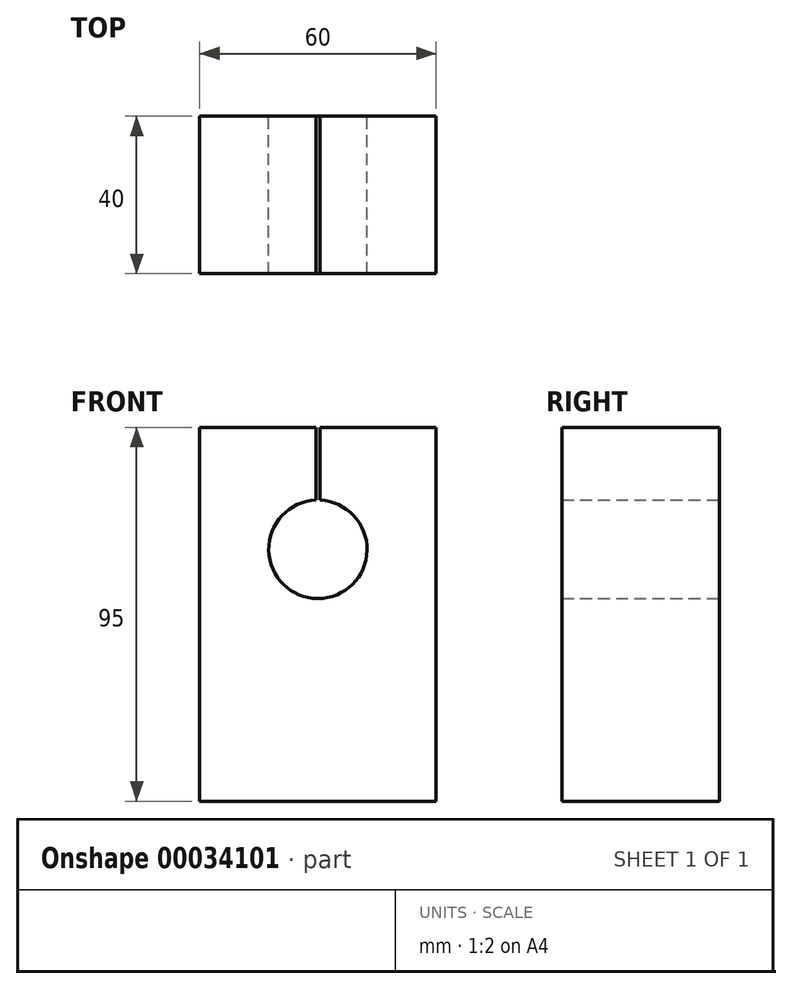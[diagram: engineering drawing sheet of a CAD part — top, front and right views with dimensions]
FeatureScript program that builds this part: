
annotation { "Feature Type Name" : "Feature", "Feature Type Description" : "" }
export const myFeature = defineFeature(function(context is Context, id is Id, definition is map)
    precondition{}
    {
        {
            var Q0;
            Q0=qCreatedBy(makeId("Front.planeOp"),FACE);
            var sketch = newSketch(context, id + "F0", { "sketchPlane" : qUnion([Q0])});
            skLineSegment(sketch, "E0.bottom", {"start": v(-30, 0) * mm, "end": v(30, 0) * mm});
            skLineSegment(sketch, "E0.top", {"start": v(-30, 95) * mm, "end": v(-0.5, 95) * mm});
            skLineSegment(sketch, "E0.left", {"start": v(-30, 0) * mm, "end": v(-30, 95) * mm});
            skLineSegment(sketch, "E0.right", {"start": v(30, 0) * mm, "end": v(30, 95) * mm});
            skArc(sketch, "E1", {"start": v(-0.5, 76.49) * mm, "mid": v(0, 51.5) * mm, "end": v(0.5, 76.49) * mm});
            skLineSegment(sketch, "E2", {"start": v(-0.5, 95) * mm, "end": v(-0.5, 76.49) * mm});
            skLineSegment(sketch, "E3.MirrorCS", {"start": v(0.5, 95) * mm, "end": v(0.5, 76.49) * mm});
            skLineSegment(sketch, "E4.trimOffspring", {"start": v(0.5, 95) * mm, "end": v(30, 95) * mm});
            skSolve(sketch);
        }
        {
            var Q0;
            Q0=qSketchRegion(id+"F0",true);
            extrude(context, id + "F1", {"entities" : qUnion([Q0]), "depth" : 40 * mm});
        }
    });
